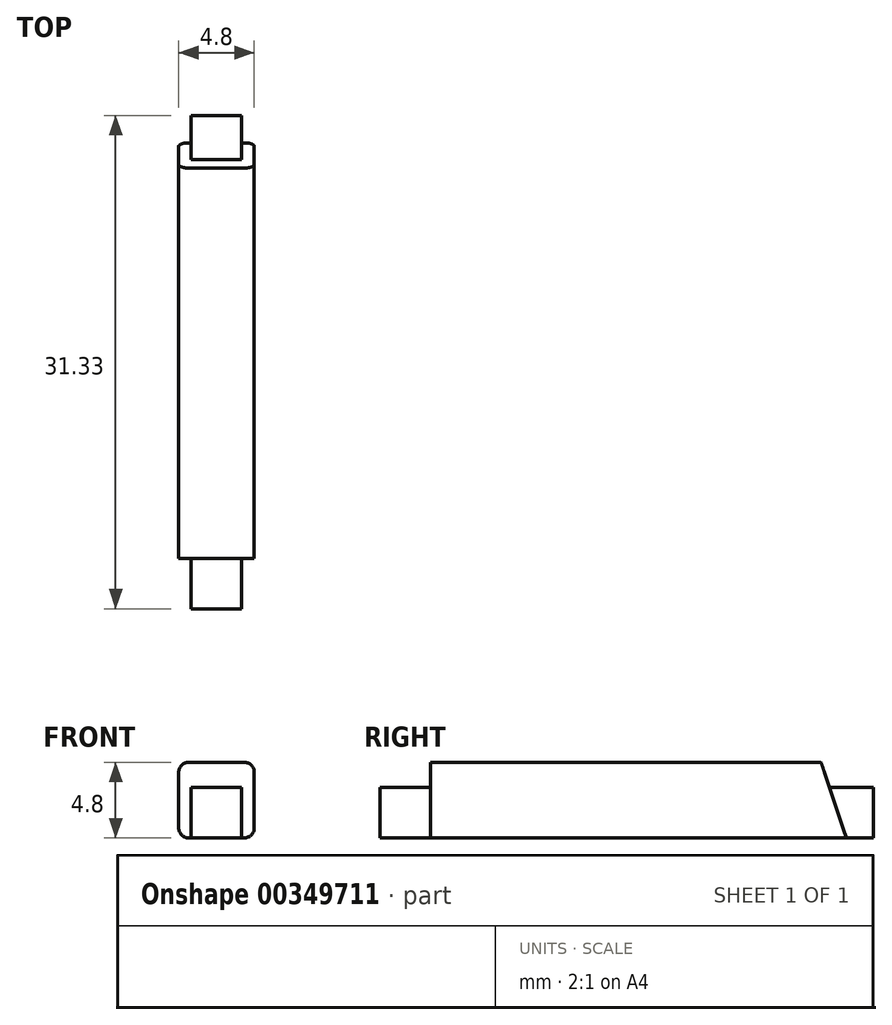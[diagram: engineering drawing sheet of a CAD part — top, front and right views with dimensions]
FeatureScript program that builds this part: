
annotation { "Feature Type Name" : "Feature", "Feature Type Description" : "" }
export const myFeature = defineFeature(function(context is Context, id is Id, definition is map)
    precondition{}
    {
        {
            var Q0;
            Q0=qCreatedBy(makeId("Top.planeOp"),FACE);
            var sketch = newSketch(context, id + "F0", { "sketchPlane" : qUnion([Q0])});
            skLineSegment(sketch, "E0.bottom", {"start": v(3, -25) * mm, "end": v(-3, -25) * mm});
            skLineSegment(sketch, "E0.top", {"start": v(3, 25) * mm, "end": v(-3, 25) * mm});
            skLineSegment(sketch, "E0.left", {"start": v(3, -25) * mm, "end": v(3, 25) * mm});
            skLineSegment(sketch, "E0.right", {"start": v(-3, -25) * mm, "end": v(-3, 25) * mm});
            skPoint(sketch, "E0.middle", {"position": v(0, 0) * mm});
            skSolve(sketch);
        }
        {
            var Q0;
            Q0 = qSketchRegion(id + "F0", true);
            extrude(context, id + "F1", {"entities" : qUnion([Q0]), "depth" : 6 * mm});
        }
        {
            var Q0;
            Q0=makeQuery(id+"F1.opExtrude","SWEPT_FACE",FACE,{"disambiguationData":[OSD([sQuery(id+"F0.wireOp",EDGE,"E0.bottom")])]});
            var sketch = newSketch(context, id + "F2", { "sketchPlane" : qUnion([Q0])});
            skLineSegment(sketch, "E1", {"start": v(-3, 0) * mm, "end": v(-2, 0) * mm});
            skLineSegment(sketch, "E2.bottom", {"start": v(-2, 0) * mm, "end": v(2, 0) * mm});
            skLineSegment(sketch, "E2.top", {"start": v(-2, 4) * mm, "end": v(2, 4) * mm});
            skLineSegment(sketch, "E2.left", {"start": v(-2, 0) * mm, "end": v(-2, 4) * mm});
            skLineSegment(sketch, "E2.right", {"start": v(2, 0) * mm, "end": v(2, 4) * mm});
            skSolve(sketch);
        }
        {
            var Q0;
            Q0=makeQuery(id+"F2.imprint","IMPRINT",FACE,{"disambiguationData":[TD([[makeQuery(id+"F2.imprint","IMPRINT",EDGE,{"derivedFrom":sQuery(id+"F2.wireOp",EDGE,"E2.bottom")}),-1.0]])]});
            extrude(context, id + "F3", {"entities" : qUnion([Q0]), "operationType" : NewBodyOperationType.ADD, "depth" : 5 * mm});
        }
        {
            var Q0;
            Q0=makeQuery(id+"F1.opExtrude","SWEPT_FACE",FACE,{"disambiguationData":[OSD([sQuery(id+"F0.wireOp",EDGE,"E0.right")])]});
            var sketch = newSketch(context, id + "F4", { "sketchPlane" : qUnion([Q0])});
            skLineSegment(sketch, "E3", {"start": v(-25, 0) * mm, "end": v(-23, 0) * mm});
            skLineSegment(sketch, "E4", {"start": v(-23, 0) * mm, "end": v(-25, 6) * mm});
            skSolve(sketch);
        }
        {
            var Q0;
            Q0 = qSketchRegion(id + "F4", true);
            var Q1;
            Q1=makeQuery(id+"F4.imprint","IMPRINT",FACE,{"disambiguationData":[TD([[makeQuery(id+"F4.imprint","IMPRINT",EDGE,{"derivedFrom":sQuery(id+"F4.wireOp",EDGE,"E3")}),-1.0]])]});
            extrude(context, id + "F5", {"entities" : qUnion([Q0, Q1]), "operationType" : NewBodyOperationType.REMOVE, "oppositeDirection" : true, "depth" : 1 * mm});
        }
        {
            var Q0;
            Q0=makeQuery(id+"F1.opExtrude","SWEPT_FACE",FACE,{"disambiguationData":[OSD([sQuery(id+"F0.wireOp",EDGE,"E0.left")])]});
            var sketch = newSketch(context, id + "F6", { "sketchPlane" : qUnion([Q0])});
            skLineSegment(sketch, "E5", {"start": v(25, 0) * mm, "end": v(23, 0) * mm});
            skLineSegment(sketch, "E6", {"start": v(23, 0) * mm, "end": v(25, 6) * mm});
            skLineSegment(sketch, "E7", {"start": v(25, 6) * mm, "end": v(25, 0) * mm});
            skSolve(sketch);
        }
        {
            var Q0;
            Q0 = qSketchRegion(id + "F6", true);
            extrude(context, id + "F7", {"entities" : qUnion([Q0]), "operationType" : NewBodyOperationType.REMOVE, "oppositeDirection" : true, "depth" : 1 * mm});
        }
        {
            var Q0;
            Q0=makeQuery(id+"F1.opExtrude","SWEPT_FACE",FACE,{"disambiguationData":[OSD([sQuery(id+"F0.wireOp",EDGE,"E0.top")])]});
            extrude(context, id + "F8", {"entities" : qUnion([Q0]), "operationType" : NewBodyOperationType.ADD, "depth" : 4 * mm});
        }
        {
            var Q0;
            {var subQ0=sQuery(id+"F6.wireOp",EDGE,"E7");Q0=makeQuery(id+"F8.boolean.opBoolean","MERGE",FACE,{"derivedFrom":[makeQuery(id+"F7.boolean.opBoolean","COPY",FACE,{"derivedFrom":makeQuery(id+"F7.opExtrude","CAP_FACE",FACE,{"disambiguationData":[OSD([sQuery(id+"F6.wireOp",EDGE,"E5"),sQuery(id+"F6.wireOp",EDGE,"E6"),subQ0])],"isStart":false})}),makeQuery(id+"F8.opExtrude","SWEPT_FACE",FACE,{"disambiguationData":[OSD([subQ0])]})]});}
            var sketch = newSketch(context, id + "F9", { "sketchPlane" : qUnion([Q0])});
            skLineSegment(sketch, "E8", {"start": v(23, 0) * mm, "end": v(26.5, 0) * mm});
            skLineSegment(sketch, "E9", {"start": v(26.5, 0) * mm, "end": v(26.5, 4) * mm});
            skLineSegment(sketch, "E10", {"start": v(26.5, 4) * mm, "end": v(24.33, 4) * mm});
            skSolve(sketch);
        }
        {
            var Q0;
            {var subQ5=sQuery(id+"F9.wireOp",EDGE,"E9");Q0=makeQuery(id+"F9.imprint","IMPRINT",FACE,{"disambiguationData":[TD([[makeQuery(id+"F9.imprint","IMPRINT",EDGE,{"derivedFrom":subQ5}),-1.0]])]});}
            extrude(context, id + "F10", {"entities" : qUnion([Q0]), "operationType" : NewBodyOperationType.REMOVE, "oppositeDirection" : true, "depth" : 25 * mm});
        }
        {
            var Q0;
            Q0=makeQuery(id+"F3.opExtrude","SWEPT_FACE",FACE,{"disambiguationData":[OSD([sQuery(id+"F2.wireOp",EDGE,"E2.left")])]});
            var sketch = newSketch(context, id + "F11", { "sketchPlane" : qUnion([Q0])});
            skLineSegment(sketch, "E11", {"start": v(30, 4) * mm, "end": v(29, 4) * mm});
            skLineSegment(sketch, "E12", {"start": v(29, 4) * mm, "end": v(29, 0) * mm});
            skSolve(sketch);
        }
        {
            var Q0;
            Q0=makeQuery(id+"F11.imprint","IMPRINT",FACE,{"disambiguationData":[TD([[makeQuery(id+"F11.imprint","IMPRINT",EDGE,{"derivedFrom":sQuery(id+"F11.wireOp",EDGE,"E11")}),1.0]])]});
            extrude(context, id + "F12", {"entities" : qUnion([Q0]), "operationType" : NewBodyOperationType.REMOVE, "oppositeDirection" : true, "depth" : 25 * mm});
        }
        {
            var Q0;
            Q0=makeQuery(id+"F1.opExtrude","SWEPT_FACE",FACE,{"disambiguationData":[OSD([sQuery(id+"F0.wireOp",EDGE,"E0.bottom")])]});
            extrude(context, id + "F13", {"entities" : qUnion([Q0]), "operationType" : NewBodyOperationType.REMOVE, "oppositeDirection" : true, "depth" : 15 * mm});
        }
        {
            var Q0;
            Q0=makeQuery(id+"F12.boolean.opBoolean","COPY",FACE,{"derivedFrom":makeQuery(id+"F12.opExtrude","SWEPT_FACE",FACE,{"disambiguationData":[OSD([sQuery(id+"F11.wireOp",EDGE,"E12")])]})});
            extrude(context, id + "F14", {"entities" : qUnion([Q0]), "operationType" : NewBodyOperationType.REMOVE, "oppositeDirection" : true, "depth" : 15 * mm});
        }
        {
            var Q0;
            Q0=makeQuery(id+"F1.opExtrude","SWEPT_FACE",FACE,{"disambiguationData":[OSD([sQuery(id+"F0.wireOp",EDGE,"E0.left")])]});
            var sketch = newSketch(context, id + "F15", { "sketchPlane" : qUnion([Q0])});
            skLineSegment(sketch, "E13", {"start": v(25, 6) * mm, "end": v(21, 6) * mm});
            skLineSegment(sketch, "E14", {"start": v(21, 6) * mm, "end": v(23, 0) * mm});
            skSolve(sketch);
        }
        {
            var Q0;
            Q0 = qSketchRegion(id + "F15", true);
            var Q1;
            Q1=makeQuery(id+"F15.imprint","IMPRINT",FACE,{"disambiguationData":[TD([[makeQuery(id+"F15.imprint","IMPRINT",EDGE,{"derivedFrom":sQuery(id+"F15.wireOp",EDGE,"E13")}),-1.0]])]});
            extrude(context, id + "F16", {"entities" : qUnion([Q0, Q1]), "operationType" : NewBodyOperationType.REMOVE, "oppositeDirection" : true, "depth" : 1 * mm});
        }
        {
            var Q0;
            Q0=makeQuery(id+"F1.opExtrude","SWEPT_FACE",FACE,{"disambiguationData":[OSD([sQuery(id+"F0.wireOp",EDGE,"E0.right")])]});
            var sketch = newSketch(context, id + "F17", { "sketchPlane" : qUnion([Q0])});
            skLineSegment(sketch, "E15", {"start": v(-25, 6) * mm, "end": v(-21, 6) * mm});
            skLineSegment(sketch, "E16", {"start": v(-21, 6) * mm, "end": v(-23, 0) * mm});
            skSolve(sketch);
        }
        {
            var Q0;
            Q0 = qSketchRegion(id + "F17", true);
            var Q1;
            Q1=makeQuery(id+"F17.imprint","IMPRINT",FACE,{"disambiguationData":[TD([[makeQuery(id+"F17.imprint","IMPRINT",EDGE,{"derivedFrom":sQuery(id+"F17.wireOp",EDGE,"E15")}),1.0]])]});
            extrude(context, id + "F18", {"entities" : qUnion([Q0, Q1]), "operationType" : NewBodyOperationType.REMOVE, "oppositeDirection" : true, "depth" : 1 * mm});
        }
        {
            var Q0;
            {var subQ0=sQuery(id+"F4.wireOp",EDGE,"E4");var subQ1=sQuery(id+"F0.wireOp",EDGE,"E0.right");var subQ2=sQuery(id+"F0.wireOp",EDGE,"E0.top");Q0=makeQuery(id+"F18.boolean.opBoolean","MERGE",FACE,{"derivedFrom":[makeQuery(id+"F8.boolean.opBoolean","MERGE",FACE,{"derivedFrom":[makeQuery(id+"F5.boolean.opBoolean","COPY",FACE,{"derivedFrom":makeQuery(id+"F5.opExtrude","CAP_FACE",FACE,{"disambiguationData":[OSD([subQ2,subQ1,sQuery(id+"F4.wireOp",EDGE,"E3"),subQ0])],"isStart":false})}),makeQuery(id+"F8.opExtrude","SWEPT_FACE",FACE,{"disambiguationData":[OSD([subQ2,subQ1])]})]}),makeQuery(id+"F18.opExtrude","CAP_FACE",FACE,{"disambiguationData":[OSD([subQ0,sQuery(id+"F17.wireOp",EDGE,"E15"),sQuery(id+"F17.wireOp",EDGE,"E16")])],"isStart":false})]});}
            var sketch = newSketch(context, id + "F19", { "sketchPlane" : qUnion([Q0])});
            skLineSegment(sketch, "E17", {"start": v(-24.33, 4) * mm, "end": v(-21.67, 4) * mm});
            skSolve(sketch);
        }
        {
            var Q0;
            Q0 = qSketchRegion(id + "F19", true);
            var Q1;
            {var subQ0=sQuery(id+"F19.wireOp",EDGE,"E17");Q1=makeQuery(id+"F19.imprint","IMPRINT",FACE,{"disambiguationData":[TD([[makeQuery(id+"F19.imprint","IMPRINT",EDGE,{"derivedFrom":subQ0}),1.0]])]});}
            extrude(context, id + "F20", {"entities" : qUnion([Q0, Q1]), "operationType" : NewBodyOperationType.REMOVE, "oppositeDirection" : true, "depth" : 4 * mm});
        }
        {
            var Q0;
            Q0=makeQuery(id+"F10.boolean.opBoolean","COPY",FACE,{"derivedFrom":makeQuery(id+"F10.opExtrude","SWEPT_FACE",FACE,{"disambiguationData":[OSD([sQuery(id+"F9.wireOp",EDGE,"E9")])]})});
            extrude(context, id + "F21", {"entities" : qUnion([Q0]), "operationType" : NewBodyOperationType.REMOVE, "oppositeDirection" : true, "depth" : 1.33 * mm});
        }
        {
            var Q0;
            Q0=makeQuery(id+"F1.opExtrude","CAP_EDGE",EDGE,{"disambiguationData":[OSD([sQuery(id+"F0.wireOp",EDGE,"E0.left")])],"isStart":false});
            var Q1;
            Q1=makeQuery(id+"F1.opExtrude","CAP_EDGE",EDGE,{"disambiguationData":[OSD([sQuery(id+"F0.wireOp",EDGE,"E0.left")])],"isStart":true});
            var Q2;
            Q2=makeQuery(id+"F1.opExtrude","CAP_EDGE",EDGE,{"disambiguationData":[OSD([sQuery(id+"F0.wireOp",EDGE,"E0.right")])],"isStart":false});
            var Q3;
            Q3=makeQuery(id+"F1.opExtrude","CAP_EDGE",EDGE,{"disambiguationData":[OSD([sQuery(id+"F0.wireOp",EDGE,"E0.right")])],"isStart":true});
            fillet(context, id + "F22", {"entities" : qUnion([Q0, Q1, Q2, Q3]), "radius" : .8 * mm, "tangentPropagation" : true, "allowEdgeOverflow" : false});
        }
        {
            var Q0;
            Q0=makeQuery(id+"F1.opExtrude","SWEPT_BODY",BODY,{"disambiguationData":[OSD([sQuery(id+"F0.wireOp",EDGE,"E0.bottom"),sQuery(id+"F0.wireOp",EDGE,"E0.top"),sQuery(id+"F0.wireOp",EDGE,"E0.left"),sQuery(id+"F0.wireOp",EDGE,"E0.right")])]});
            var Q1;
            Q1=qCreatedBy(makeId("Origin.pointOp"),VERTEX);
            transform(context, id + "F23", {"entities" : qUnion([Q0]), "transformType" : TransformType.SCALE_UNIFORMLY, "scale" : .8, "scalePoint" : qUnion([Q1]), "makeCopy" : false});
        }
    });
